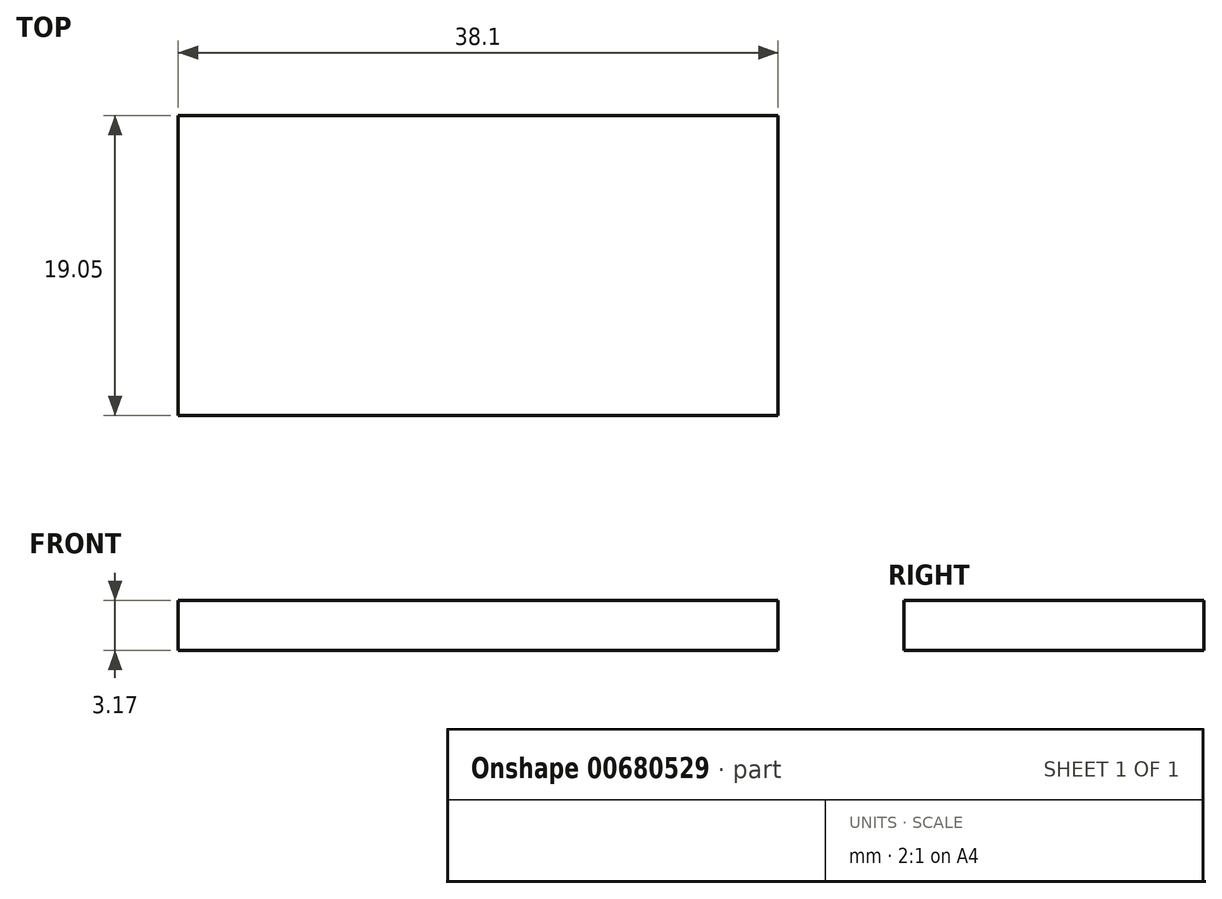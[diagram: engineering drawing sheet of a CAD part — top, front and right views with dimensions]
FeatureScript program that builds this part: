
annotation { "Feature Type Name" : "Feature", "Feature Type Description" : "" }
export const myFeature = defineFeature(function(context is Context, id is Id, definition is map)
    precondition{}
    {
        {
            var Q0;
            Q0=qCreatedBy(makeId("Top.planeOp"),FACE);
            var sketch = newSketch(context, id + "F0", { "sketchPlane" : qUnion([Q0])});
            skLineSegment(sketch, "E0.bottom", {"start": v(0, 0) * mm, "end": v(-38.1, 0) * mm});
            skLineSegment(sketch, "E0.top", {"start": v(0, 19.05) * mm, "end": v(-38.1, 19.05) * mm});
            skLineSegment(sketch, "E0.left", {"start": v(0, 0) * mm, "end": v(0, 19.05) * mm});
            skLineSegment(sketch, "E0.right", {"start": v(-38.1, 0) * mm, "end": v(-38.1, 19.05) * mm});
            skSolve(sketch);
        }
        {
            var Q0;
            Q0 = qSketchRegion(id + "F0", true);
            extrude(context, id + "F1", {"entities" : qUnion([Q0]), "depth" : 3.17 * mm, "offsetDistance" : 25.4 * mm});
        }
    });
